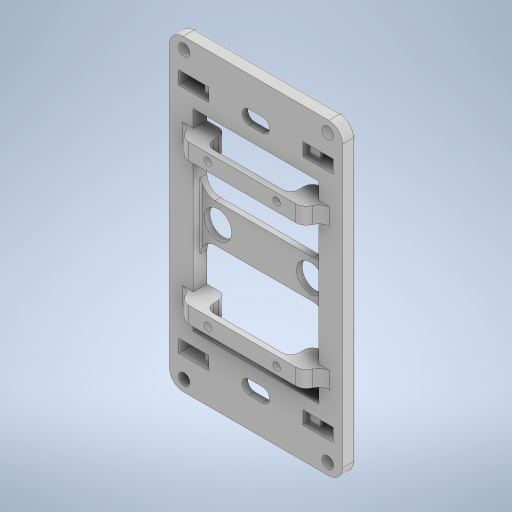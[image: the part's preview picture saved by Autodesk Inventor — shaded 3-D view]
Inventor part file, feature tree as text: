
AUTODESK INVENTOR PART (.ipt)
format: ipt  version: 2023 (Build 270158000, 158)  size: 523,264 bytes
history: native  units: mm
features: extrude x9, fillet x7, sketch x7, mirror x3, other x2, projected_geometry x1
ambient origin geometry x8: Origin, YZ Plane, XZ Plane, XY Plane, X Axis, Y Axis, Z Axis, Center Point
bodies: Body1 (feature_tree)
feature tree (29):
  other  "솔리드1"
  extrude  "돌출1"  Depth=63.1mm
  extrude  "돌출2"  Depth=112.2mm
  extrude  "돌출3"  Depth=45.85mm
  fillet  "모깎기1"  Radius=70.23mm
  sketch  "스케치4"
  extrude  "돌출4"  Depth=5.0mm TaperAngle=0.0deg
  extrude  "돌출5"  Depth=5.0mm
  mirror  "미러1"
  mirror  "미러2"
  extrude  "돌출6"  Depth=5.0mm
  fillet  "모깎기2"  Radius=5.0mm
  mirror  "미러3"
  fillet  "모깎기3"  Radius=10.0mm
  extrude  "돌출7"  Depth=104.0mm
  fillet  "모깎기4"  Radius=4.2mm
  fillet  "모깎기5"  Radius=52.4mm
  other  "작업 평면1"
  sketch  "스케치9"
  extrude  "돌출8"  TaperAngle=0.0deg  [1 undecoded]
  extrude  "돌출9"  Depth=5.0mm
  fillet  "모깎기6"  Radius=7.0mm
  fillet  "모깎기7"  Radius=4.7mm
  sketch  "스케치1"
  sketch  "스케치2"
  sketch  "스케치3"
  sketch  "스케치6"
  projected_geometry  "투영된 루프1"
  sketch  "스케치8"
note: 1 required parameter value undecoded (feature->parameter linkage not recoverable at this tier; creation-order binding heuristic only, values carry confidence <= 0.55)
